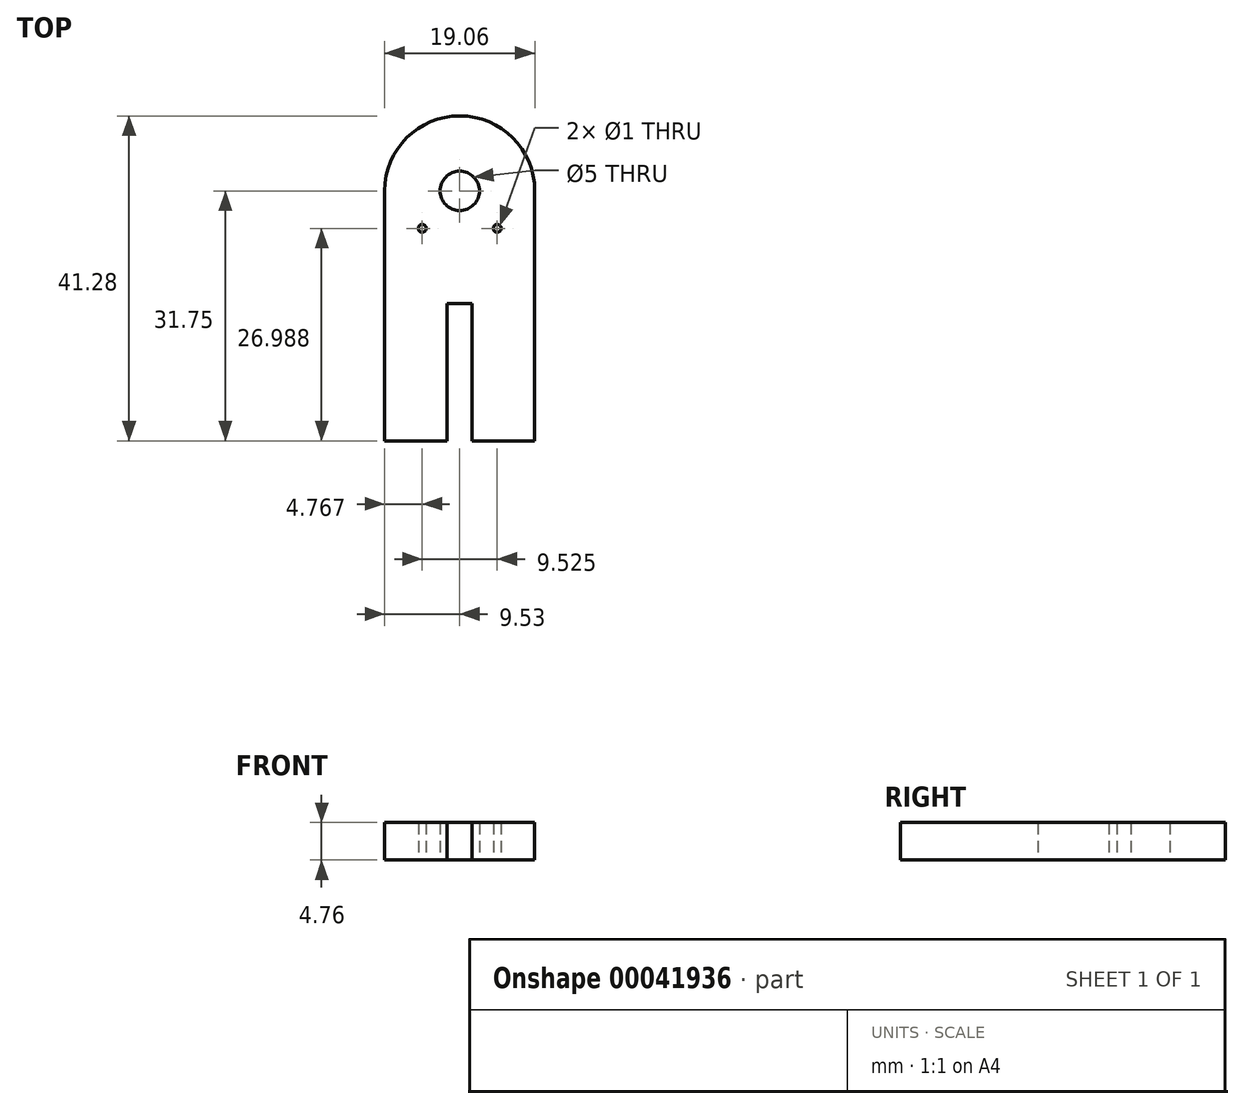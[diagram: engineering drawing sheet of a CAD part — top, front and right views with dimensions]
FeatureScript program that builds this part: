
annotation { "Feature Type Name" : "Feature", "Feature Type Description" : "" }
export const myFeature = defineFeature(function(context is Context, id is Id, definition is map)
    precondition{}
    {
        {
            var Q0;
            Q0=qCreatedBy(makeId("Top.planeOp"),FACE);
            var sketch = newSketch(context, id + "F0", { "sketchPlane" : qUnion([Q0])});
            skArc(sketch, "E0", {"start": v(9.53, 0) * mm, "mid": v(0, 9.53) * mm, "end": v(-9.53, 0) * mm});
            skLineSegment(sketch, "E1", {"start": v(-9.53, 0) * mm, "end": v(-9.53, -31.75) * mm});
            skLineSegment(sketch, "E2", {"start": v(9.53, 0) * mm, "end": v(9.53, -31.75) * mm});
            skCircle(sketch, "E3", {"center": v(0, 0) * mm, "radius": 2.5 * mm});
            skLineSegment(sketch, "E4", {"start": v(-1.59, -31.75) * mm, "end": v(-1.59, -14.29) * mm});
            skLineSegment(sketch, "E5", {"start": v(1.59, -31.75) * mm, "end": v(1.59, -14.29) * mm});
            skLineSegment(sketch, "E6", {"start": v(-1.59, -14.29) * mm, "end": v(1.59, -14.29) * mm});
            skLineSegment(sketch, "E7", {"start": v(-1.59, -31.75) * mm, "end": v(-9.53, -31.75) * mm});
            skLineSegment(sketch, "E8", {"start": v(1.59, -31.75) * mm, "end": v(9.53, -31.75) * mm});
            skCircle(sketch, "E9", {"center": v(-4.76, -4.76) * mm, "radius": 0.5 * mm});
            skCircle(sketch, "E10.MirrorC", {"center": v(4.76, -4.76) * mm, "radius": 0.5 * mm});
            skSolve(sketch);
        }
        {
            var Q0;
            Q0=makeQuery(id+"F0.imprint","IMPRINT",FACE,{"disambiguationData":[TD([[makeQuery(id+"F0.imprint","IMPRINT",EDGE,{"derivedFrom":sQuery(id+"F0.wireOp",EDGE,"E0")}),1.0]])]});
            extrude(context, id + "F1", {"entities" : qUnion([Q0]), "depth" : 4.76 * mm});
        }
    });
